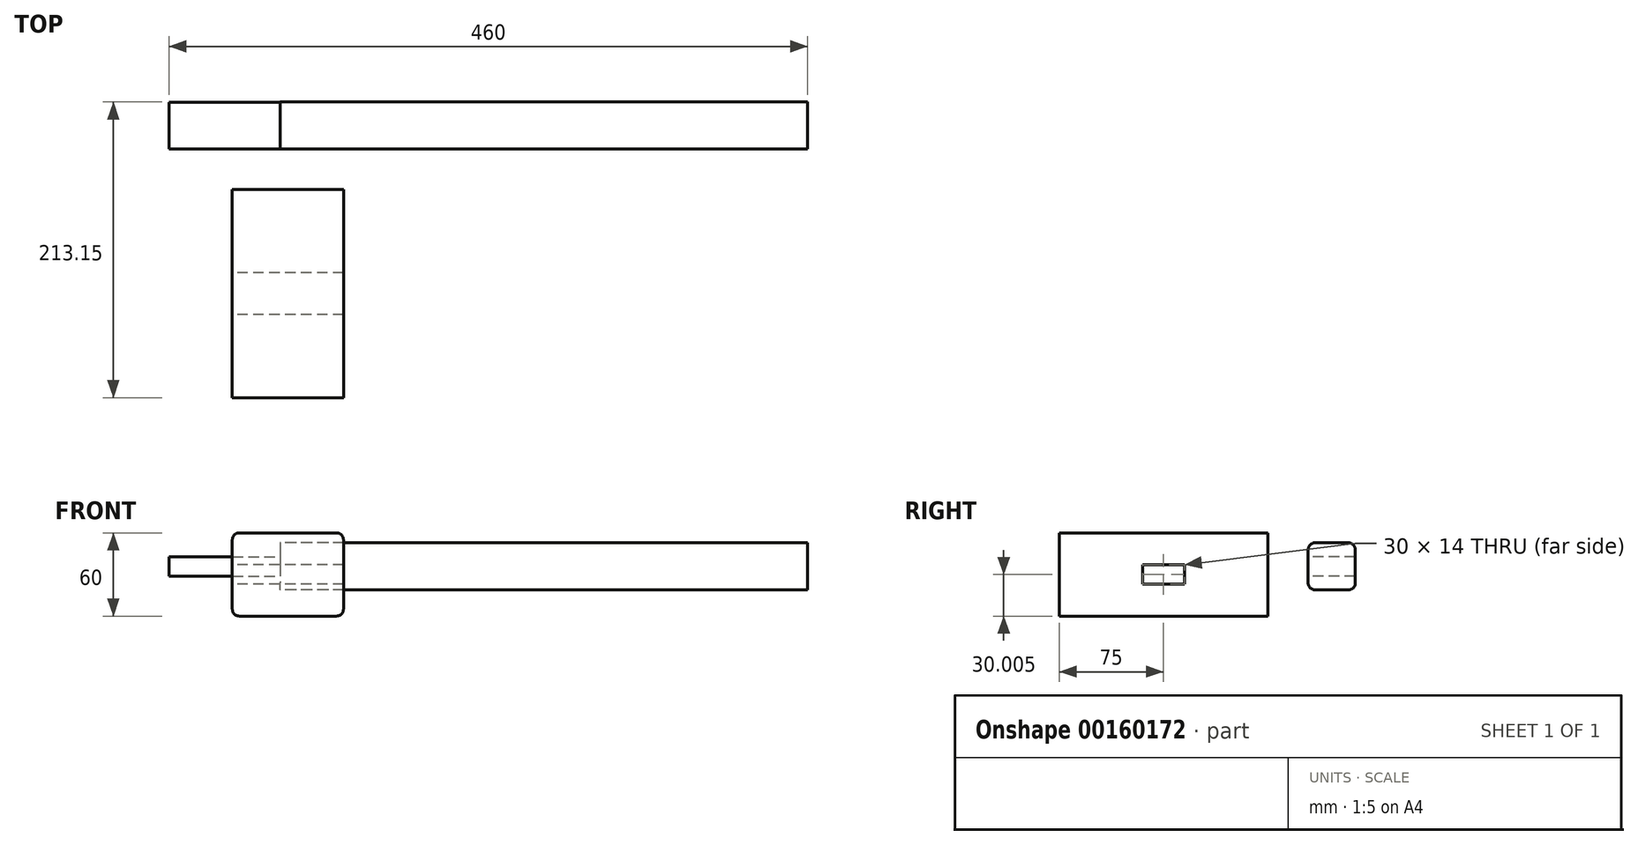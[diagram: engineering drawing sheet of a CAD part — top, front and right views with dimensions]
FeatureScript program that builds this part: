
annotation { "Feature Type Name" : "Feature", "Feature Type Description" : "" }
export const myFeature = defineFeature(function(context is Context, id is Id, definition is map)
    precondition{}
    {
        {
            var Q0;
            Q0=qCreatedBy(makeId("Front.planeOp"),FACE);
            var sketch = newSketch(context, id + "F0", { "sketchPlane" : qUnion([Q0])});
            skLineSegment(sketch, "E0.bottom", {"start": v(-34.28, 22.67) * mm, "end": v(45.72, 22.67) * mm});
            skLineSegment(sketch, "E0.top", {"start": v(-34.28, -37.33) * mm, "end": v(45.72, -37.33) * mm});
            skLineSegment(sketch, "E0.left", {"start": v(-34.28, 22.67) * mm, "end": v(-34.28, -37.33) * mm});
            skLineSegment(sketch, "E0.right", {"start": v(45.72, 22.67) * mm, "end": v(45.72, -37.33) * mm});
            skSolve(sketch);
        }
        {
            var Q0;
            Q0 = qSketchRegion(id + "F0", true);
            extrude(context, id + "F1", {"entities" : qUnion([Q0]), "depth" : 150 * mm});
        }
        {
            var Q0;
            Q0=makeQuery(id+"F1.opExtrude","SWEPT_FACE",FACE,{"disambiguationData":[OSD([sQuery(id+"F0.wireOp",EDGE,"E0.left")])]});
            var sketch = newSketch(context, id + "F2", { "sketchPlane" : qUnion([Q0])});
            skLineSegment(sketch, "E1.bottom", {"start": v(90, -14.33) * mm, "end": v(60, -14.33) * mm});
            skLineSegment(sketch, "E1.top", {"start": v(90, -0.33) * mm, "end": v(60, -0.33) * mm});
            skLineSegment(sketch, "E1.left", {"start": v(90, -14.33) * mm, "end": v(90, -0.33) * mm});
            skLineSegment(sketch, "E1.right", {"start": v(60, -14.33) * mm, "end": v(60, -0.33) * mm});
            skPoint(sketch, "E1.middle", {"position": v(75, -7.33) * mm});
            skPoint(sketch, "E2", {"position": v(75, -37.33) * mm});
            skSolve(sketch);
        }
        {
            var Q0;
            Q0 = qSketchRegion(id + "F2", true);
            extrude(context, id + "F3", {"entities" : qUnion([Q0]), "operationType" : NewBodyOperationType.REMOVE, "endBound" : BoundingType.THROUGH_ALL, "oppositeDirection" : true, "depth" : 25 * mm});
        }
        {
            var Q0;
            Q0=qCreatedBy(makeId("Right.planeOp"),FACE);
            var sketch = newSketch(context, id + "F4", { "sketchPlane" : qUnion([Q0])});
            skLineSegment(sketch, "E3.bottom", {"start": v(29.15, 15.55) * mm, "end": v(63.15, 15.55) * mm});
            skLineSegment(sketch, "E3.top", {"start": v(29.15, -18.45) * mm, "end": v(63.15, -18.45) * mm});
            skLineSegment(sketch, "E3.left", {"start": v(29.15, 15.55) * mm, "end": v(29.15, -18.45) * mm});
            skLineSegment(sketch, "E3.right", {"start": v(63.15, 15.55) * mm, "end": v(63.15, -18.45) * mm});
            skSolve(sketch);
        }
        {
            var Q0;
            Q0 = qSketchRegion(id + "F4", true);
            extrude(context, id + "F5", {"entities" : qUnion([Q0]), "depth" : 380 * mm});
        }
        {
            var Q0;
            Q0=makeQuery(id+"F5.opExtrude","SWEPT_EDGE",EDGE,{"disambiguationData":[OSD([sQuery(id+"F4.wireOp",EDGE,"E3.bottom"),sQuery(id+"F4.wireOp",EDGE,"E3.right")])]});
            var Q1;
            Q1=makeQuery(id+"F5.opExtrude","SWEPT_EDGE",EDGE,{"disambiguationData":[OSD([sQuery(id+"F4.wireOp",EDGE,"E3.bottom"),sQuery(id+"F4.wireOp",EDGE,"E3.left")])]});
            var Q2;
            Q2=makeQuery(id+"F5.opExtrude","SWEPT_EDGE",EDGE,{"disambiguationData":[OSD([sQuery(id+"F4.wireOp",EDGE,"E3.top"),sQuery(id+"F4.wireOp",EDGE,"E3.left")])]});
            var Q3;
            Q3=makeQuery(id+"F5.opExtrude","SWEPT_EDGE",EDGE,{"disambiguationData":[OSD([sQuery(id+"F4.wireOp",EDGE,"E3.top"),sQuery(id+"F4.wireOp",EDGE,"E3.right")])]});
            var Q4;
            Q4=makeQuery(id+"F1.opExtrude","SWEPT_EDGE",EDGE,{"disambiguationData":[OSD([sQuery(id+"F0.wireOp",EDGE,"E0.top"),sQuery(id+"F0.wireOp",EDGE,"E0.right")])]});
            var Q5;
            Q5=makeQuery(id+"F1.opExtrude","SWEPT_EDGE",EDGE,{"disambiguationData":[OSD([sQuery(id+"F0.wireOp",EDGE,"E0.top"),sQuery(id+"F0.wireOp",EDGE,"E0.left")])]});
            var Q6;
            Q6=makeQuery(id+"F1.opExtrude","SWEPT_EDGE",EDGE,{"disambiguationData":[OSD([sQuery(id+"F0.wireOp",EDGE,"E0.bottom"),sQuery(id+"F0.wireOp",EDGE,"E0.left")])]});
            var Q7;
            Q7=makeQuery(id+"F1.opExtrude","SWEPT_EDGE",EDGE,{"disambiguationData":[OSD([sQuery(id+"F0.wireOp",EDGE,"E0.bottom"),sQuery(id+"F0.wireOp",EDGE,"E0.right")])]});
            fillet(context, id + "F6", {"entities" : qUnion([Q0, Q1, Q2, Q3, Q4, Q5, Q6, Q7]), "radius" : 5 * mm, "tangentPropagation" : true, "allowEdgeOverflow" : false});
        }
        {
            var Q0;
            Q0=makeQuery(id+"F4.imprint","IMPRINT",FACE,{"disambiguationData":[TD([[makeQuery(id+"F4.imprint","IMPRINT",EDGE,{"derivedFrom":sQuery(id+"F4.wireOp",EDGE,"E3.bottom")}),-1.0]])]});
            var sketch = newSketch(context, id + "F7", { "sketchPlane" : qUnion([Q0])});
            skPoint(sketch, "E4", {"position": v(46.15, -1.45) * mm});
            skLineSegment(sketch, "E5.bottom", {"start": v(63.03, 5.55) * mm, "end": v(29.27, 5.55) * mm});
            skLineSegment(sketch, "E5.top", {"start": v(63.03, -8.45) * mm, "end": v(29.27, -8.45) * mm});
            skLineSegment(sketch, "E5.left", {"start": v(63.03, 5.55) * mm, "end": v(63.03, -8.45) * mm});
            skLineSegment(sketch, "E5.right", {"start": v(29.27, 5.55) * mm, "end": v(29.27, -8.45) * mm});
            skSolve(sketch);
        }
        {
            var Q0;
            Q0 = qSketchRegion(id + "F7", true);
            extrude(context, id + "F8", {"entities" : qUnion([Q0]), "operationType" : NewBodyOperationType.ADD, "oppositeDirection" : true, "depth" : 80 * mm});
        }
    });
